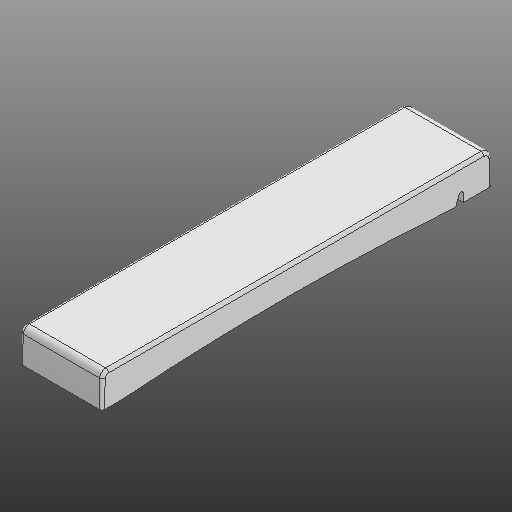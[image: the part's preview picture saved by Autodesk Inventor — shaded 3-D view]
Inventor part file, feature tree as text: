
AUTODESK INVENTOR PART (.ipt)
format: ipt  version: 2020 (Build 240168000, 168)  size: 309,248 bytes
history: native  units: in
note: dims shown in document units (in); Inventor stores cm internally (conversion verified against a paired STEP export)
features: extrude x4, other x3, fillet x2
ambient origin geometry x8: Origin, YZ Plane, XZ Plane, XY Plane, X Axis, Y Axis, Z Axis, Center Point
bodies: Solid1 (feature_tree)
feature tree (9):
  other  "Slot Start Plane"
  other  "Key Profile"
  extrude  "Upper (u)"  TaperAngle=0.0deg  [1 undecoded]
  extrude  "Lower (d)"  TaperAngle=0.0deg  [1 undecoded]
  extrude  "Protrusion Cutout"  Depth=0.0591in
  fillet  "Front Fillet"  Radius=0.1374in
  extrude  "Slot"  [1 undecoded]
  fillet  "Edge Softening"  Radius=0.0787in
  other  "Slot Sketch"
note: 3 required parameter values undecoded (feature->parameter linkage not recoverable at this tier; creation-order binding heuristic only, values carry confidence <= 0.55)
